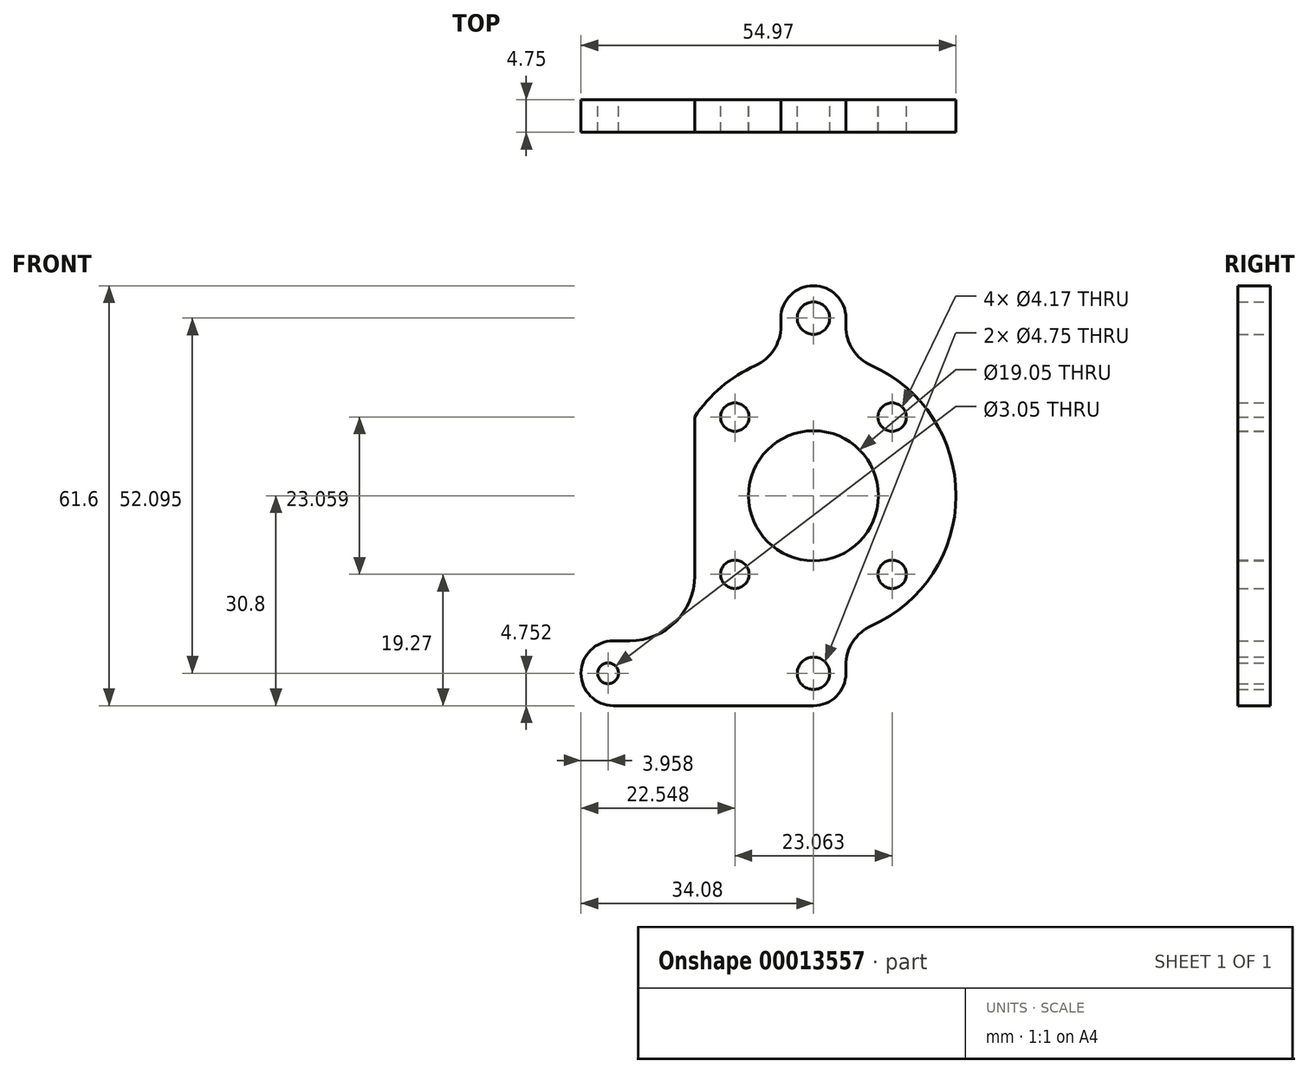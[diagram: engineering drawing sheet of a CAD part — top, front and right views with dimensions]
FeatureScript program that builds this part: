
annotation { "Feature Type Name" : "Feature", "Feature Type Description" : "" }
export const myFeature = defineFeature(function(context is Context, id is Id, definition is map)
    precondition{}
    {
        {
            var Q0;
            Q0=qCreatedBy(makeId("Front.planeOp"),FACE);
            var sketch = newSketch(context, id + "F0", { "sketchPlane" : qUnion([Q0])});
            skCircle(sketch, "E0", {"center": v(0, 0) * mm, "radius": 9.53 * mm});
            skCircle(sketch, "E1", {"center": v(11.53, 11.53) * mm, "radius": 2.08 * mm});
            skCircle(sketch, "E2", {"center": v(11.53, -11.53) * mm, "radius": 2.08 * mm});
            skCircle(sketch, "E3", {"center": v(-11.53, -11.53) * mm, "radius": 2.08 * mm});
            skCircle(sketch, "E4", {"center": v(-11.53, 11.53) * mm, "radius": 2.08 * mm});
            skCircle(sketch, "E5", {"center": v(0, 26.05) * mm, "radius": 2.37 * mm});
            skCircle(sketch, "E6", {"center": v(0, -26.05) * mm, "radius": 2.37 * mm});
            skLineSegment(sketch, "E7", {"start": v(-4.78, 20.34) * mm, "end": v(-4.78, 30.8) * mm});
            skLineSegment(sketch, "E8", {"start": v(-4.78, 30.8) * mm, "end": v(4.75, 30.8) * mm});
            skLineSegment(sketch, "E9", {"start": v(4.75, 30.8) * mm, "end": v(4.75, 20.34) * mm});
            skLineSegment(sketch, "E10", {"start": v(-4.78, -30.8) * mm, "end": v(4.75, -30.8) * mm});
            skLineSegment(sketch, "E11", {"start": v(4.75, -30.8) * mm, "end": v(4.75, -20.34) * mm});
            skArc(sketch, "E12.trimOffspring", {"start": v(-4.78, 20.34) * mm, "mid": v(-11.94, 17.14) * mm, "end": v(-17.42, 11.53) * mm});
            skArc(sketch, "E13.trimOffspring", {"start": v(4.75, -20.34) * mm, "mid": v(20.9, 0) * mm, "end": v(4.75, 20.34) * mm});
            skPoint(sketch, "E14.center.orphan", {"position": v(-30.12, 0) * mm});
            skCircle(sketch, "E15", {"center": v(-30.12, -26.05) * mm, "radius": 1.52 * mm});
            skLineSegment(sketch, "E16", {"start": v(-4.78, -30.8) * mm, "end": v(-34.08, -30.8) * mm});
            skLineSegment(sketch, "E17", {"start": v(-34.08, -30.8) * mm, "end": v(-34.08, -21.27) * mm});
            skLineSegment(sketch, "E18", {"start": v(-34.08, -21.27) * mm, "end": v(-17.42, -21.27) * mm});
            skLineSegment(sketch, "E19", {"start": v(-17.42, -21.27) * mm, "end": v(-17.42, -11.53) * mm});
            skLineSegment(sketch, "E20", {"start": v(-17.42, 11.53) * mm, "end": v(-17.42, -11.53) * mm});
            skSolve(sketch);
        }
        {
            var Q0;
            Q0=makeQuery(id+"F0.imprint","IMPRINT",FACE,{"disambiguationData":[TD([[makeQuery(id+"F0.imprint","IMPRINT",EDGE,{"derivedFrom":sQuery(id+"F0.wireOp",EDGE,"E0")}),-1.0]])]});
            extrude(context, id + "F1", {"entities" : qUnion([Q0]), "depth" : 4.75 * mm});
        }
        {
            var Q0;
            Q0=makeQuery(id+"F1.opExtrude","SWEPT_EDGE",EDGE,{"disambiguationData":[OSD([sQuery(id+"F0.wireOp",EDGE,"E7"),sQuery(id+"F0.wireOp",EDGE,"E8")])]});
            var Q1;
            Q1=makeQuery(id+"F1.opExtrude","SWEPT_EDGE",EDGE,{"disambiguationData":[OSD([sQuery(id+"F0.wireOp",EDGE,"E8"),sQuery(id+"F0.wireOp",EDGE,"E9")])]});
            var Q2;
            Q2=makeQuery(id+"F1.opExtrude","SWEPT_EDGE",EDGE,{"disambiguationData":[OSD([sQuery(id+"F0.wireOp",EDGE,"E10"),sQuery(id+"F0.wireOp",EDGE,"E11")])]});
            var Q3;
            Q3=makeQuery(id+"F1.opExtrude","SWEPT_EDGE",EDGE,{"disambiguationData":[OSD([sQuery(id+"F0.wireOp",EDGE,"2547cd51-214c-4e8f-8c8b-9297974fec82"),sQuery(id+"F0.wireOp",EDGE,"E10")])]});
            fillet(context, id + "F2", {"entities" : qUnion([Q0, Q1, Q2, Q3]), "radius" : 4.75 * mm, "tangentPropagation" : true, "allowEdgeOverflow" : false});
        }
        {
            var Q0;
            Q0=makeQuery(id+"F1.opExtrude","SWEPT_EDGE",EDGE,{"disambiguationData":[OSD([sQuery(id+"F0.wireOp",EDGE,"e7cd79d1-08eb-4f04-b5be-c058e0ed79c2"),sQuery(id+"F0.wireOp",EDGE,"86d0a385-4206-48b5-943c-631c5e1fc730")])]});
            var Q1;
            Q1=makeQuery(id+"F1.opExtrude","SWEPT_EDGE",EDGE,{"disambiguationData":[OSD([sQuery(id+"F0.wireOp",EDGE,"feffe153-c6bd-49d7-8783-758cbaba38a2"),sQuery(id+"F0.wireOp",EDGE,"dfc2a04d-d897-4ba0-bdb2-bd18dc863bc0.trimOffspring")])]});
            var Q2;
            Q2=makeQuery(id+"F1.opExtrude","SWEPT_EDGE",EDGE,{"disambiguationData":[OSD([sQuery(id+"F0.wireOp",EDGE,"E7"),sQuery(id+"F0.wireOp",EDGE,"E12.trimOffspring")])]});
            var Q3;
            Q3=makeQuery(id+"F1.opExtrude","SWEPT_EDGE",EDGE,{"disambiguationData":[OSD([sQuery(id+"F0.wireOp",EDGE,"E9"),sQuery(id+"F0.wireOp",EDGE,"E13.trimOffspring")])]});
            var Q4;
            Q4=makeQuery(id+"F1.opExtrude","SWEPT_EDGE",EDGE,{"disambiguationData":[OSD([sQuery(id+"F0.wireOp",EDGE,"E11"),sQuery(id+"F0.wireOp",EDGE,"E13.trimOffspring")])]});
            var Q5;
            Q5=makeQuery(id+"F1.opExtrude","SWEPT_EDGE",EDGE,{"disambiguationData":[OSD([sQuery(id+"F0.wireOp",EDGE,"bf3a03c1-f540-45f3-982a-c349b05721b9"),sQuery(id+"F0.wireOp",EDGE,"2547cd51-214c-4e8f-8c8b-9297974fec82")])]});
            fillet(context, id + "F3", {"entities" : qUnion([Q0, Q1, Q2, Q3, Q4, Q5]), "radius" : 6.35 * mm, "tangentPropagation" : true, "allowEdgeOverflow" : false});
        }
        {
            var Q0;
            Q0=makeQuery(id+"F1.opExtrude","SWEPT_EDGE",EDGE,{"disambiguationData":[OSD([sQuery(id+"F0.wireOp",EDGE,"E18"),sQuery(id+"F0.wireOp",EDGE,"E19")])]});
            fillet(context, id + "F4", {"entities" : qUnion([Q0]), "radius" : 9.52 * mm, "tangentPropagation" : true, "allowEdgeOverflow" : false});
        }
        {
            var Q0;
            Q0=makeQuery(id+"F1.opExtrude","SWEPT_EDGE",EDGE,{"disambiguationData":[OSD([sQuery(id+"F0.wireOp",EDGE,"E17"),sQuery(id+"F0.wireOp",EDGE,"E18")])]});
            var Q1;
            Q1=makeQuery(id+"F1.opExtrude","SWEPT_EDGE",EDGE,{"disambiguationData":[OSD([sQuery(id+"F0.wireOp",EDGE,"E16"),sQuery(id+"F0.wireOp",EDGE,"E17")])]});
            fillet(context, id + "F5", {"entities" : qUnion([Q0, Q1]), "radius" : 4.76 * mm, "tangentPropagation" : true, "allowEdgeOverflow" : false});
        }
    });
